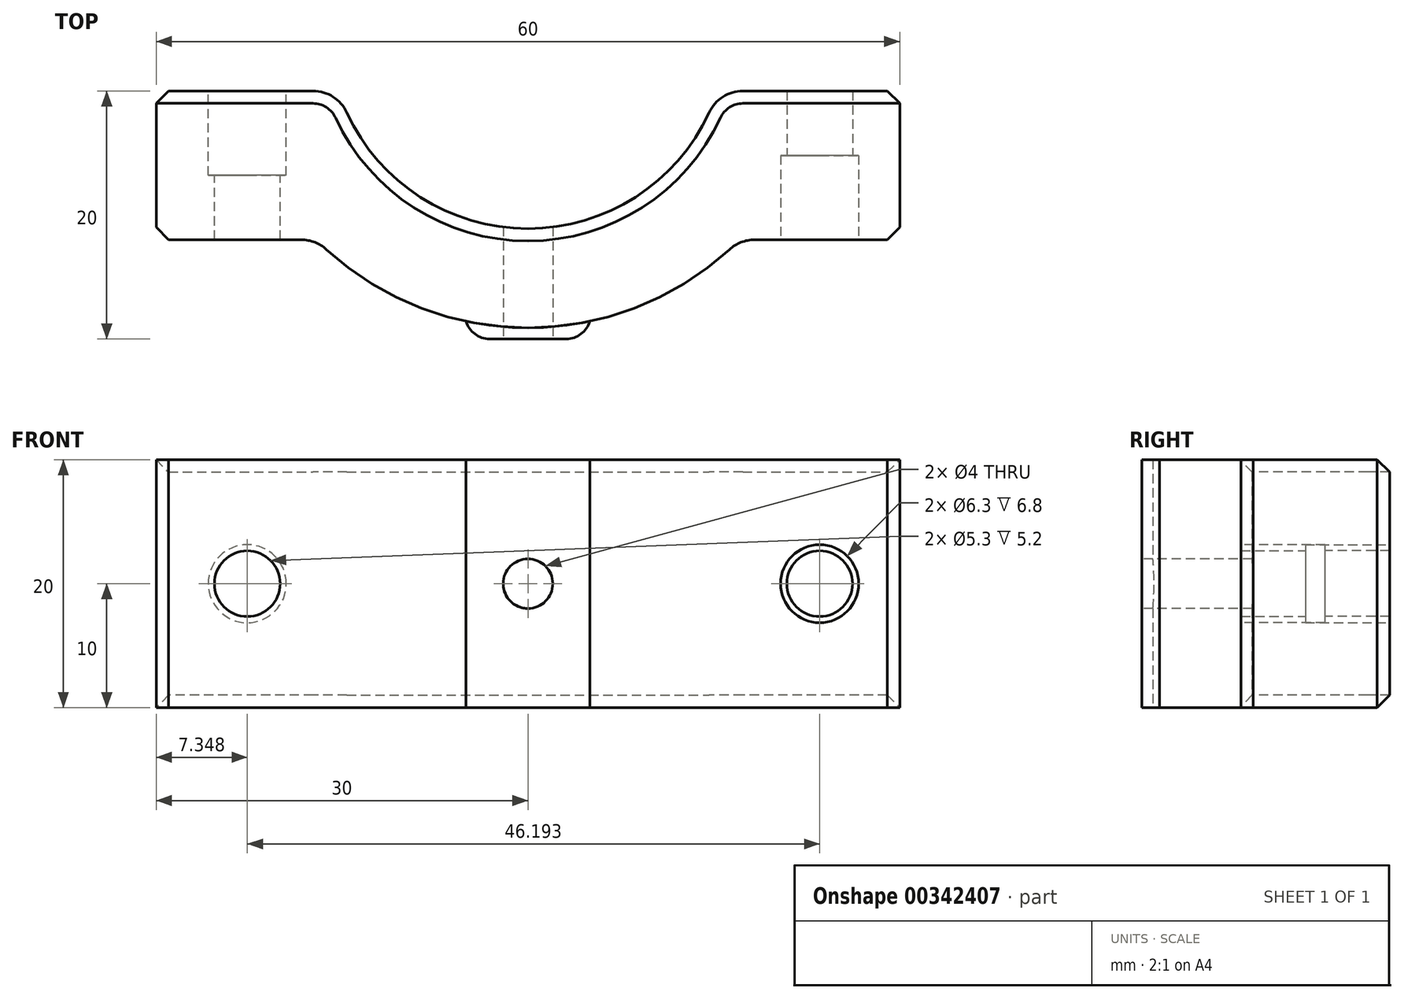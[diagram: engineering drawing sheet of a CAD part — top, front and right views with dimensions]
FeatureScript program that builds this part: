
annotation { "Feature Type Name" : "Feature", "Feature Type Description" : "" }
export const myFeature = defineFeature(function(context is Context, id is Id, definition is map)
    precondition{}
    {
        {
            var Q0;
            Q0=qCreatedBy(makeId("Top.planeOp"),FACE);
            var sketch = newSketch(context, id + "F0", { "sketchPlane" : qUnion([Q0])});
            skArc(sketch, "E0", {"start": v(-15.3, -5) * mm, "mid": v(0, -16.1) * mm, "end": v(15.3, -5) * mm});
            skLineSegment(sketch, "E1", {"start": v(-30, -5) * mm, "end": v(-15.3, -5) * mm});
            skLineSegment(sketch, "E2", {"start": v(-30, -5) * mm, "end": v(-30, -17) * mm});
            skLineSegment(sketch, "E3", {"start": v(30, -5) * mm, "end": v(30, -17) * mm});
            skArc(sketch, "E4.0", {"start": v(-17.08, -17) * mm, "mid": v(0, -24.1) * mm, "end": v(17.08, -17) * mm});
            skLineSegment(sketch, "E5.trimOffspring", {"start": v(15.3, -5) * mm, "end": v(30, -5) * mm});
            skLineSegment(sketch, "E6", {"start": v(-30, -17) * mm, "end": v(-17.08, -17) * mm});
            skLineSegment(sketch, "E7", {"start": v(30, -17) * mm, "end": v(17.08, -17) * mm});
            skSolve(sketch);
        }
        {
            var Q0;
            Q0=makeQuery(id+"F0.imprint","IMPRINT",FACE,{"disambiguationData":[TD([[makeQuery(id+"F0.imprint","IMPRINT",EDGE,{"derivedFrom":sQuery(id+"F0.wireOp",EDGE,"E0")}),-1.0]])]});
            extrude(context, id + "F1", {"entities" : qUnion([Q0]), "depth" : 20 * mm});
        }
        {
            var Q0;
            Q0=makeQuery(id+"F1.opExtrude","SWEPT_FACE",FACE,{"disambiguationData":[OSD([sQuery(id+"F0.wireOp",EDGE,"E7")])]});
            var sketch = newSketch(context, id + "F2", { "sketchPlane" : qUnion([Q0])});
            skCircle(sketch, "E8", {"center": v(23.54, 10) * mm, "radius": 3.15 * mm});
            skSolve(sketch);
        }
        {
            var Q0;
            Q0 = qSketchRegion(id + "F2", true);
            extrude(context, id + "F3", {"entities" : qUnion([Q0]), "operationType" : NewBodyOperationType.REMOVE, "oppositeDirection" : true, "depth" : 6.8 * mm});
        }
        {
            var Q0;
            Q0=makeQuery(id+"F3.boolean.opBoolean","COPY",FACE,{"derivedFrom":makeQuery(id+"F3.opExtrude","CAP_FACE",FACE,{"disambiguationData":[OSD([sQuery(id+"F2.wireOp",EDGE,"E8")])],"isStart":false})});
            var sketch = newSketch(context, id + "F4", { "sketchPlane" : qUnion([Q0])});
            skCircle(sketch, "E9", {"center": v(23.54, 10) * mm, "radius": 2.65 * mm});
            skSolve(sketch);
        }
        {
            var Q0;
            Q0 = qSketchRegion(id + "F4", true);
            extrude(context, id + "F5", {"entities" : qUnion([Q0]), "operationType" : NewBodyOperationType.REMOVE, "endBound" : BoundingType.UP_TO_NEXT, "oppositeDirection" : true, "depth" : 25 * mm});
        }
        {
            var Q0;
            Q0=makeQuery(id+"F1.opExtrude","SWEPT_FACE",FACE,{"disambiguationData":[OSD([sQuery(id+"F0.wireOp",EDGE,"E1")])]});
            var sketch = newSketch(context, id + "F6", { "sketchPlane" : qUnion([Q0])});
            skCircle(sketch, "E10", {"center": v(22.65, 10) * mm, "radius": 3.15 * mm});
            skPoint(sketch, "E10.centerSnap0", {"position": v(15.3, 10) * mm});
            skSolve(sketch);
        }
        {
            var Q0;
            Q0 = qSketchRegion(id + "F6", true);
            extrude(context, id + "F7", {"entities" : qUnion([Q0]), "operationType" : NewBodyOperationType.REMOVE, "oppositeDirection" : true, "depth" : 6.8 * mm});
        }
        {
            var Q0;
            Q0=makeQuery(id+"F7.boolean.opBoolean","COPY",FACE,{"derivedFrom":makeQuery(id+"F7.opExtrude","CAP_FACE",FACE,{"disambiguationData":[OSD([sQuery(id+"F6.wireOp",EDGE,"E10")])],"isStart":false})});
            var sketch = newSketch(context, id + "F8", { "sketchPlane" : qUnion([Q0])});
            skCircle(sketch, "E11", {"center": v(22.65, 10) * mm, "radius": 2.65 * mm});
            skSolve(sketch);
        }
        {
            var Q0;
            Q0 = qSketchRegion(id + "F8", true);
            extrude(context, id + "F9", {"entities" : qUnion([Q0]), "operationType" : NewBodyOperationType.REMOVE, "endBound" : BoundingType.UP_TO_NEXT, "oppositeDirection" : true, "depth" : 25 * mm});
        }
        {
            var Q0;
            Q0=qCreatedBy(makeId("Front.planeOp"),FACE);
            cPlane(context, id + "F10", {"entities" : qUnion([Q0]), "cplaneType" : CPlaneType.OFFSET, "offset" : 25 * mm, "width" : 150 * mm, "height" : 150 * mm});
        }
        {
            var Q0;
            Q0=qCreatedBy(id+"F10.planeOp",FACE);
            var sketch = newSketch(context, id + "F11", { "sketchPlane" : qUnion([Q0])});
            skLineSegment(sketch, "E12", {"start": v(0, 0) * mm, "end": v(-5, 0) * mm});
            skLineSegment(sketch, "E13", {"start": v(-5, 0) * mm, "end": v(-5, 20) * mm});
            skLineSegment(sketch, "E14", {"start": v(-5, 20) * mm, "end": v(5, 20) * mm});
            skLineSegment(sketch, "E15", {"start": v(5, 20) * mm, "end": v(5, 0) * mm});
            skLineSegment(sketch, "E16", {"start": v(5, 0) * mm, "end": v(0, 0) * mm});
            skSolve(sketch);
        }
        {
            var Q0;
            Q0 = qSketchRegion(id + "F11", true);
            extrude(context, id + "F12", {"entities" : qUnion([Q0]), "endBound" : BoundingType.UP_TO_NEXT, "oppositeDirection" : true, "depth" : 25 * mm});
        }
        {
            var Q0;
            Q0=makeQuery(id+"F12.opExtrude","CAP_FACE",FACE,{"disambiguationData":[OSD([sQuery(id+"F11.wireOp",EDGE,"E12"),sQuery(id+"F11.wireOp",EDGE,"E13"),sQuery(id+"F11.wireOp",EDGE,"E14"),sQuery(id+"F11.wireOp",EDGE,"E15"),sQuery(id+"F11.wireOp",EDGE,"E16")])],"isStart":true});
            var sketch = newSketch(context, id + "F13", { "sketchPlane" : qUnion([Q0])});
            skCircle(sketch, "E17", {"center": v(0, 10) * mm, "radius": 2 * mm});
            skPoint(sketch, "E17.centerSnap0", {"position": v(-5, 10) * mm});
            skPoint(sketch, "E18.center.orphan", {"position": v(0, 5) * mm});
            skPoint(sketch, "E19.center.orphan", {"position": v(0, 17) * mm});
            skSolve(sketch);
        }
        {
            var Q0;
            Q0 = qSketchRegion(id + "F13", true);
            extrude(context, id + "F14", {"entities" : qUnion([Q0]), "operationType" : NewBodyOperationType.REMOVE, "oppositeDirection" : true, "depth" : 30 * mm});
        }
        {
            var Q0;
            Q0=makeQuery(id+"F1.opExtrude","SWEPT_EDGE",EDGE,{"disambiguationData":[OSD([sQuery(id+"F0.wireOp",EDGE,"E0"),sQuery(id+"F0.wireOp",EDGE,"E1")])]});
            var Q1;
            Q1=makeQuery(id+"F1.opExtrude","SWEPT_EDGE",EDGE,{"disambiguationData":[OSD([sQuery(id+"F0.wireOp",EDGE,"E0"),sQuery(id+"F0.wireOp",EDGE,"E5.trimOffspring")])]});
            var Q2;
            Q2=makeQuery(id+"F1.opExtrude","SWEPT_EDGE",EDGE,{"disambiguationData":[OSD([sQuery(id+"F0.wireOp",EDGE,"E4.0"),sQuery(id+"F0.wireOp",EDGE,"E6")])]});
            var Q3;
            Q3=makeQuery(id+"F1.opExtrude","SWEPT_EDGE",EDGE,{"disambiguationData":[OSD([sQuery(id+"F0.wireOp",EDGE,"E4.0"),sQuery(id+"F0.wireOp",EDGE,"E7")])]});
            fillet(context, id + "F15", {"entities" : qUnion([Q0, Q1, Q2, Q3]), "radius" : 3 * mm, "tangentPropagation" : true, "allowEdgeOverflow" : false});
        }
        {
            var Q0;
            Q0=makeQuery(id+"F12.opExtrude","CAP_EDGE",EDGE,{"disambiguationData":[OSD([sQuery(id+"F11.wireOp",EDGE,"E13")])],"isStart":true});
            var Q1;
            Q1=makeQuery(id+"F12.opExtrude","CAP_EDGE",EDGE,{"disambiguationData":[OSD([sQuery(id+"F11.wireOp",EDGE,"E15")])],"isStart":true});
            fillet(context, id + "F16", {"entities" : qUnion([Q0, Q1]), "radius" : 2 * mm, "tangentPropagation" : true, "allowEdgeOverflow" : false});
        }
        {
            var Q0;
            Q0=makeQuery(id+"F1.opExtrude","CAP_EDGE",EDGE,{"disambiguationData":[OSD([sQuery(id+"F0.wireOp",EDGE,"E0")])],"isStart":true});
            var Q1;
            Q1=makeQuery(id+"F1.opExtrude","CAP_EDGE",EDGE,{"disambiguationData":[OSD([sQuery(id+"F0.wireOp",EDGE,"E1")])],"isStart":false});
            var Q2;
            Q2=makeQuery(id+"F1.opExtrude","SWEPT_EDGE",EDGE,{"disambiguationData":[OSD([sQuery(id+"F0.wireOp",EDGE,"E3"),sQuery(id+"F0.wireOp",EDGE,"E7")])]});
            var Q3;
            Q3=makeQuery(id+"F1.opExtrude","SWEPT_EDGE",EDGE,{"disambiguationData":[OSD([sQuery(id+"F0.wireOp",EDGE,"E2"),sQuery(id+"F0.wireOp",EDGE,"E6")])]});
            var Q4;
            Q4=makeQuery(id+"F1.opExtrude","SWEPT_EDGE",EDGE,{"disambiguationData":[OSD([sQuery(id+"F0.wireOp",EDGE,"E1"),sQuery(id+"F0.wireOp",EDGE,"E2")])]});
            var Q5;
            Q5=makeQuery(id+"F1.opExtrude","SWEPT_EDGE",EDGE,{"disambiguationData":[OSD([sQuery(id+"F0.wireOp",EDGE,"E3"),sQuery(id+"F0.wireOp",EDGE,"E5.trimOffspring")])]});
            chamfer(context, id + "F17", {"entities" : qUnion([Q0, Q1, Q2, Q3, Q4, Q5]), "width" : 1 * mm, "tangentPropagation" : true});
        }
    });
